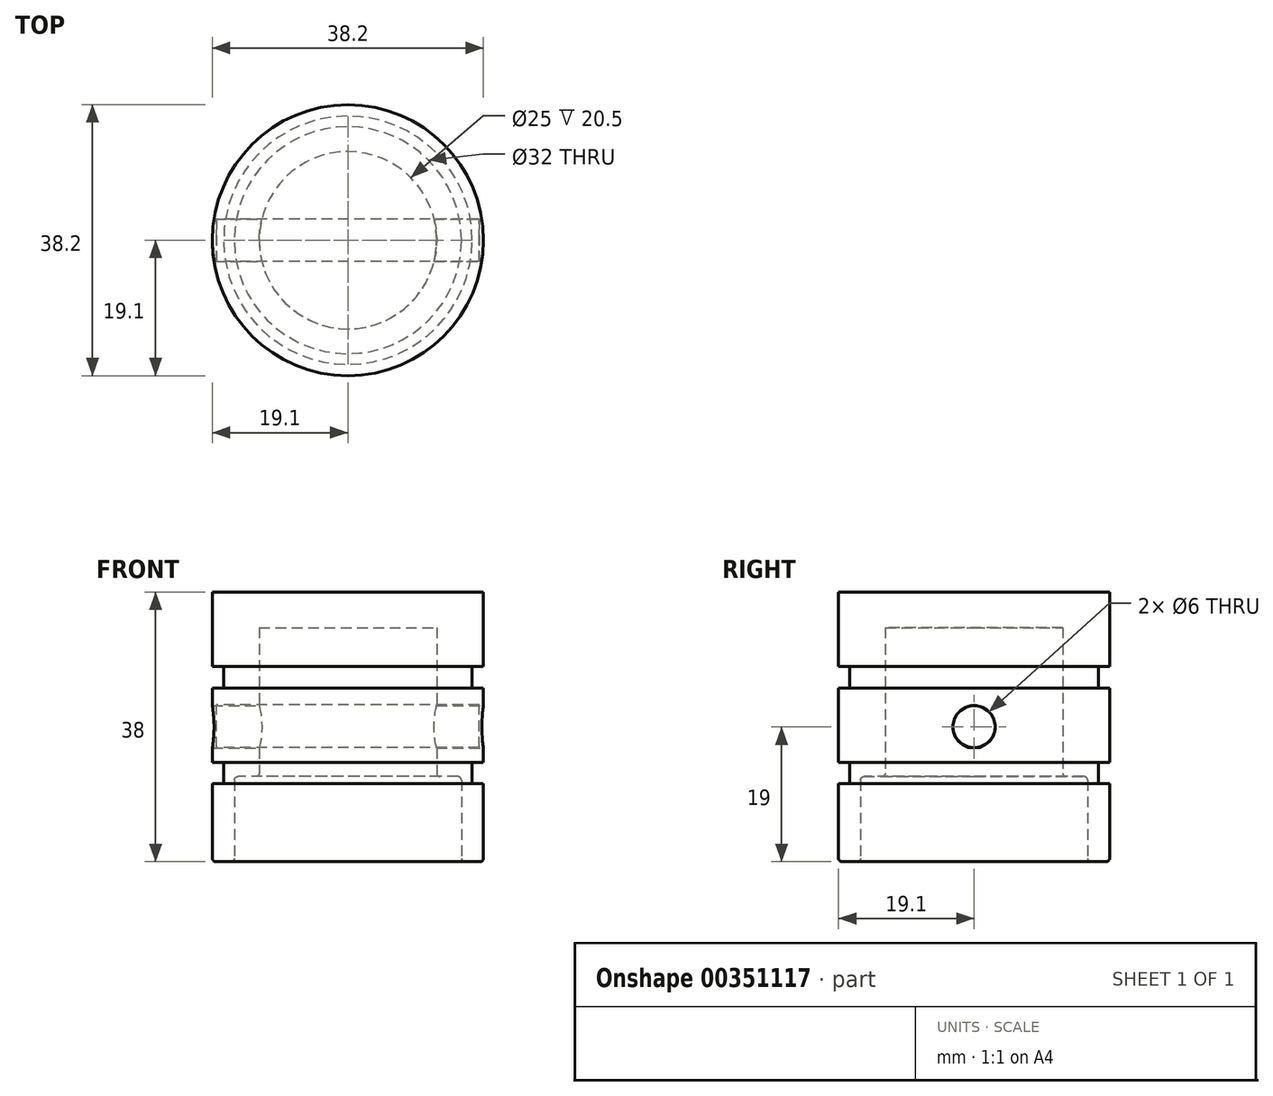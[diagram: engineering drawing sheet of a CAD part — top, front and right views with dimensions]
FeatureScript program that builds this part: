
annotation { "Feature Type Name" : "Feature", "Feature Type Description" : "" }
export const myFeature = defineFeature(function(context is Context, id is Id, definition is map)
    precondition{}
    {
        {
            var Q0;
            Q0=qCreatedBy(makeId("Right.planeOp"),FACE);
            var sketch = newSketch(context, id + "F0", { "sketchPlane" : qUnion([Q0])});
            skLineSegment(sketch, "E0", {"start": v(0, 33) * mm, "end": v(0, 38) * mm});
            skLineSegment(sketch, "E1", {"start": v(0, 38) * mm, "end": v(19.1, 38) * mm});
            skLineSegment(sketch, "E2", {"start": v(19.1, 38) * mm, "end": v(19.1, 27.5) * mm});
            skLineSegment(sketch, "E3", {"start": v(19.1, 27.5) * mm, "end": v(17.5, 27.5) * mm});
            skLineSegment(sketch, "E4", {"start": v(17.5, 27.5) * mm, "end": v(17.5, 24.5) * mm});
            skLineSegment(sketch, "E5", {"start": v(17.5, 24.5) * mm, "end": v(19.1, 24.5) * mm});
            skLineSegment(sketch, "E6", {"start": v(19.1, 24.5) * mm, "end": v(19.1, 14) * mm});
            skLineSegment(sketch, "E7", {"start": v(19.1, 14) * mm, "end": v(17.5, 14) * mm});
            skLineSegment(sketch, "E8", {"start": v(17.5, 14) * mm, "end": v(17.5, 11) * mm});
            skLineSegment(sketch, "E9", {"start": v(17.5, 11) * mm, "end": v(19.1, 11) * mm});
            skLineSegment(sketch, "E10", {"start": v(19.1, 11) * mm, "end": v(19.1, 0) * mm});
            skLineSegment(sketch, "E11", {"start": v(19.1, 0) * mm, "end": v(16, 0) * mm});
            skLineSegment(sketch, "E12", {"start": v(16, 0) * mm, "end": v(16, 12) * mm});
            skLineSegment(sketch, "E13", {"start": v(16, 12) * mm, "end": v(12.5, 12) * mm});
            skLineSegment(sketch, "E14", {"start": v(12.5, 12) * mm, "end": v(12.5, 33) * mm});
            skLineSegment(sketch, "E15", {"start": v(12.5, 33) * mm, "end": v(0, 33) * mm});
            skSolve(sketch);
        }
        {
            var Q0;
            Q0=makeQuery(id+"F0.imprint","IMPRINT",FACE,{"disambiguationData":[TD([[makeQuery(id+"F0.imprint","IMPRINT",EDGE,{"derivedFrom":sQuery(id+"F0.wireOp",EDGE,"E0")}),-1.0]])]});
            var Q1;
            Q1=sQuery(id+"F0.wireOp",EDGE,"E0");
            revolve(context, id + "F1", {"entities" : qUnion([Q0]), "axis" : qUnion([Q1]), "revolveType" : RevolveType.FULL});
        }
        {
            var Q0;
            Q0=qCreatedBy(makeId("Right.planeOp"),FACE);
            cPlane(context, id + "F2", {"entities" : qUnion([Q0]), "cplaneType" : CPlaneType.OFFSET, "offset" : 19.1 * mm, "width" : 150 * mm, "height" : 150 * mm});
        }
        {
            var Q0;
            Q0=qCreatedBy(id+"F2.planeOp",FACE);
            var sketch = newSketch(context, id + "F3", { "sketchPlane" : qUnion([Q0])});
            skCircle(sketch, "E16", {"center": v(0, 19) * mm, "radius": 3 * mm});
            skSolve(sketch);
        }
        {
            var Q0;
            Q0=makeQuery(id+"F3.imprint","IMPRINT",FACE,{"disambiguationData":[TD([[makeQuery(id+"F3.imprint","IMPRINT",EDGE,{"derivedFrom":sQuery(id+"F3.wireOp",EDGE,"E16")}),1.0]])]});
            extrude(context, id + "F4", {"entities" : qUnion([Q0]), "operationType" : NewBodyOperationType.REMOVE, "endBound" : BoundingType.THROUGH_ALL, "oppositeDirection" : true, "depth" : 25 * mm});
        }
        {
            var Q0;
            Q0=qCreatedBy(makeId("Right.planeOp"),FACE);
            var sketch = newSketch(context, id + "F5", { "sketchPlane" : qUnion([Q0])});
            skCircle(sketch, "E17", {"center": v(0, 19.1) * mm, "radius": 3 * mm});
            skSolve(sketch);
        }
        {
            var Q0;
            Q0=makeQuery(id+"F5.imprint","IMPRINT",FACE,{"disambiguationData":[TD([[makeQuery(id+"F5.imprint","IMPRINT",EDGE,{"derivedFrom":sQuery(id+"F5.wireOp",EDGE,"E17")}),1.0]])]});
            extrude(context, id + "F6", {"entities" : qUnion([Q0]), "endBound" : BoundingType.SYMMETRIC, "depth" : 37 * mm});
        }
        {
            var Q0;
            Q0=makeQuery(id+"F1.opRevolve","SWEPT_EDGE",EDGE,{"disambiguationData":[OSD([sQuery(id+"F0.wireOp",EDGE,"E10"),sQuery(id+"F0.wireOp",EDGE,"E11")])]});
            var Q1;
            Q1=makeQuery(id+"F1.opRevolve","SWEPT_EDGE",EDGE,{"disambiguationData":[OSD([sQuery(id+"F0.wireOp",EDGE,"E11"),sQuery(id+"F0.wireOp",EDGE,"E12")])]});
            var Q2;
            Q2=makeQuery(id+"F1.opRevolve","SWEPT_EDGE",EDGE,{"disambiguationData":[OSD([sQuery(id+"F0.wireOp",EDGE,"E12"),sQuery(id+"F0.wireOp",EDGE,"E13")])]});
            var Q3;
            Q3=makeQuery(id+"F1.opRevolve","SWEPT_EDGE",EDGE,{"disambiguationData":[OSD([sQuery(id+"F0.wireOp",EDGE,"E13"),sQuery(id+"F0.wireOp",EDGE,"E14")])]});
            fillet(context, id + "F7", {"entities" : qUnion([Q0, Q1, Q2, Q3]), "radius" : .5 * mm, "tangentPropagation" : true, "allowEdgeOverflow" : false});
        }
    });
